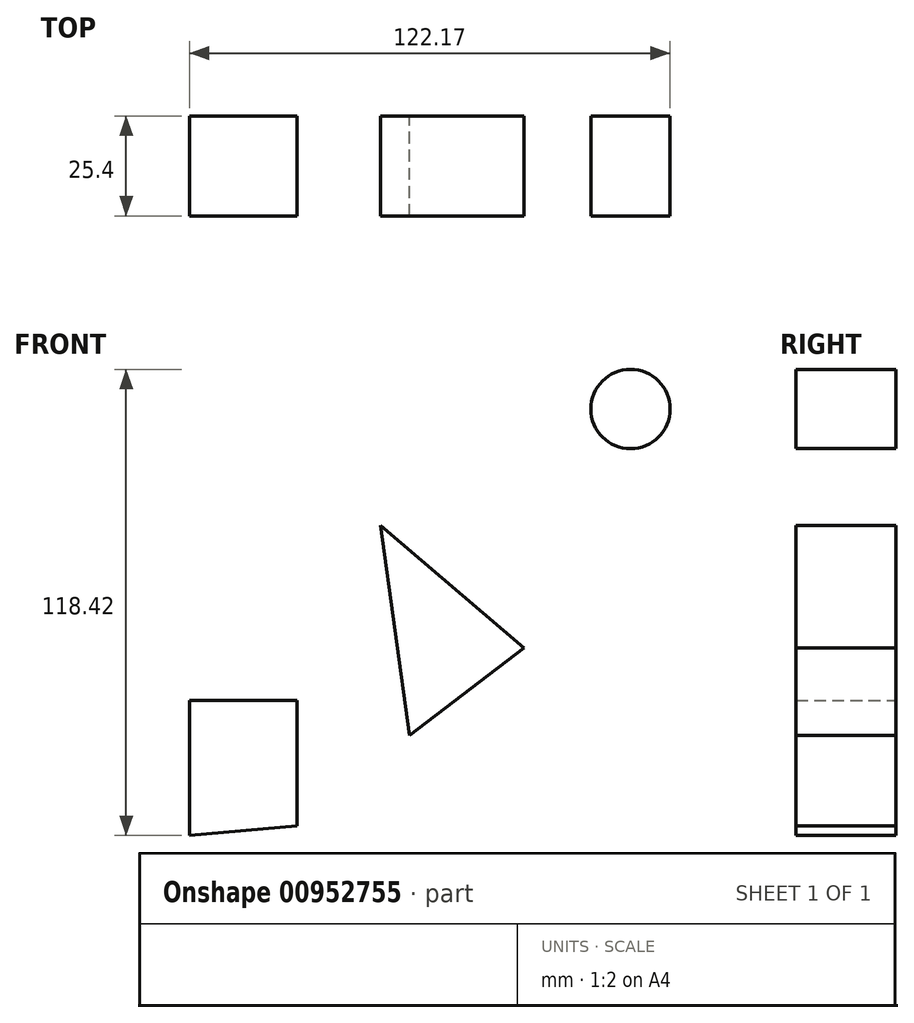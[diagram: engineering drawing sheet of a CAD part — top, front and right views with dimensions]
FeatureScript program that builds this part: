
annotation { "Feature Type Name" : "Feature", "Feature Type Description" : "" }
export const myFeature = defineFeature(function(context is Context, id is Id, definition is map)
    precondition{}
    {
        {
            var Q0;
            Q0=qCreatedBy(makeId("Front.planeOp"),FACE);
            var sketch = newSketch(context, id + "F0", { "sketchPlane" : qUnion([Q0])});
            skLineSegment(sketch, "E0", {"start": v(-54.75, 62.17) * mm, "end": v(22.37, 17.84) * mm});
            skLineSegment(sketch, "E1", {"start": v(-49.43, 0.03) * mm, "end": v(27.7, -44.3) * mm});
            skLineSegment(sketch, "E2", {"start": v(55.37, 62.79) * mm, "end": v(55.37, 18.25) * mm});
            skCircle(sketch, "E3", {"center": v(45.3, 60.73) * mm, "radius": 10.07 * mm});
            skLineSegment(sketch, "E4", {"start": v(-60.55, 43.59) * mm, "end": v(-60.55, 16.88) * mm});
            skLineSegment(sketch, "E5", {"start": v(-55.7, 43.93) * mm, "end": v(-36.28, 43.93) * mm});
            skLineSegment(sketch, "E6", {"start": v(-36.28, 43.93) * mm, "end": v(-36.28, 18.27) * mm});
            skLineSegment(sketch, "E7", {"start": v(-36.28, 18.27) * mm, "end": v(-60.55, 16.88) * mm});
            skLineSegment(sketch, "E8", {"start": v(-66.8, -13.29) * mm, "end": v(-66.8, -47.62) * mm});
            skLineSegment(sketch, "E9", {"start": v(-66.8, -13.29) * mm, "end": v(-39.4, -13.29) * mm});
            skLineSegment(sketch, "E10", {"start": v(-39.4, -13.29) * mm, "end": v(-39.4, -45.2) * mm});
            skLineSegment(sketch, "E11", {"start": v(-39.4, -45.2) * mm, "end": v(-66.8, -47.62) * mm});
            skLineSegment(sketch, "E12", {"start": v(-18.25, 31.1) * mm, "end": v(18.17, 0) * mm});
            skPoint(sketch, "E12.startSnap0", {"position": v(-36.28, 31.1) * mm});
            skLineSegment(sketch, "E13", {"start": v(-18.25, 31.1) * mm, "end": v(-10.87, -22.14) * mm});
            skLineSegment(sketch, "E14", {"start": v(18.17, 0) * mm, "end": v(-10.87, -22.14) * mm});
            skSolve(sketch);
        }
        {
            var Q0;
            Q0 = qSketchRegion(id + "F0", true);
            extrude(context, id + "F1", {"entities" : qUnion([Q0]), "depth" : 25.4 * mm, "offsetDistance" : 25.4 * mm});
        }
    });
